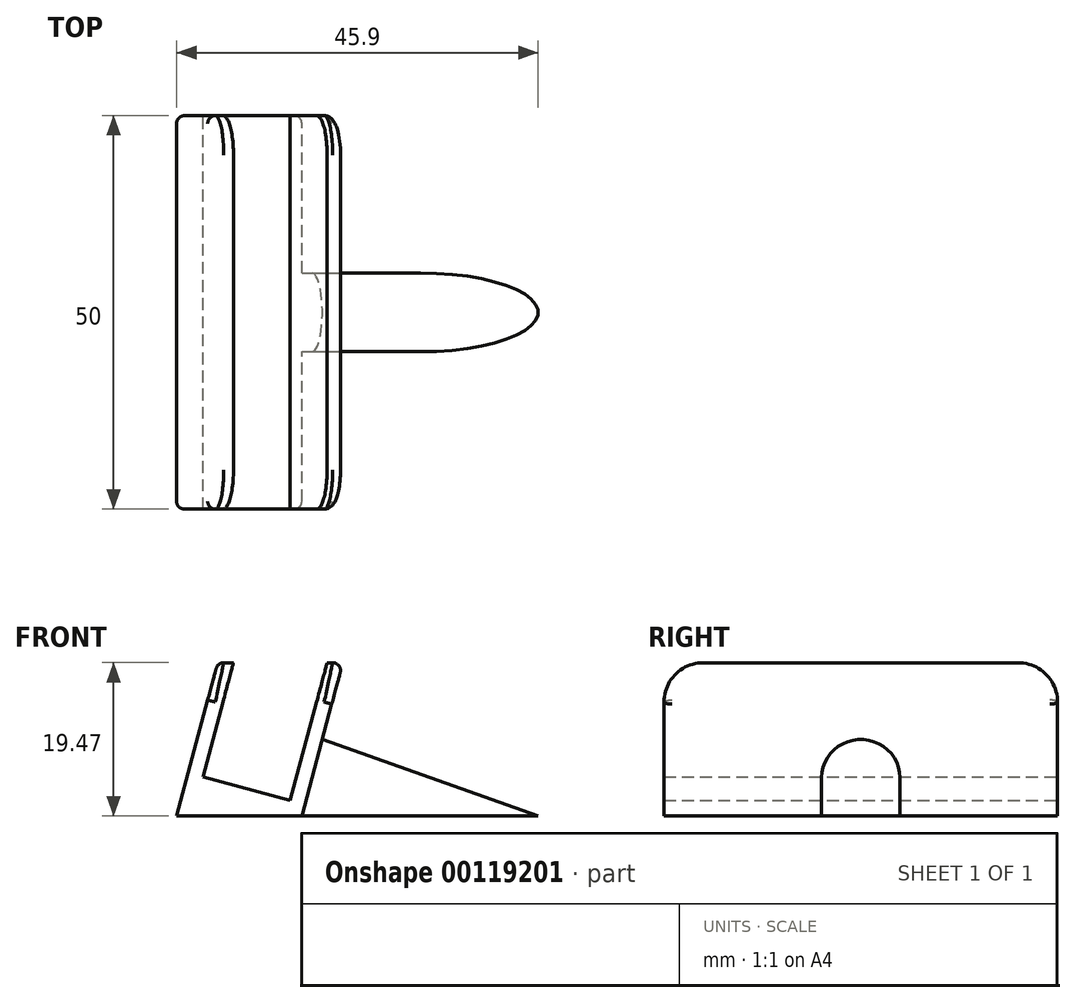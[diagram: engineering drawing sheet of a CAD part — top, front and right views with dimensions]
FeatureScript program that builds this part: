
annotation { "Feature Type Name" : "Feature", "Feature Type Description" : "" }
export const myFeature = defineFeature(function(context is Context, id is Id, definition is map)
    precondition{}
    {
        {
            var Q0;
            Q0=qCreatedBy(makeId("Front.planeOp"),FACE);
            var sketch = newSketch(context, id + "F0", { "sketchPlane" : qUnion([Q0])});
            skLineSegment(sketch, "E0", {"start": v(0, 0) * mm, "end": v(-11.1, 2.98) * mm});
            skLineSegment(sketch, "E1", {"start": v(-11.1, 2.98) * mm, "end": v(-7.23, 17.47) * mm});
            skLineSegment(sketch, "E2", {"start": v(-7.23, 17.47) * mm, "end": v(-9.23, 17.47) * mm});
            skLineSegment(sketch, "E3", {"start": v(-9.23, 17.47) * mm, "end": v(-13.9, 0) * mm});
            skLineSegment(sketch, "E4", {"start": v(4.68, 17.47) * mm, "end": v(6.68, 17.47) * mm});
            skLineSegment(sketch, "E5", {"start": v(4.68, 17.47) * mm, "end": v(0, 0) * mm});
            skLineSegment(sketch, "E6", {"start": v(-13.9, 0) * mm, "end": v(-14.44, -2) * mm});
            skLineSegment(sketch, "E7", {"start": v(-14.44, -2) * mm, "end": v(1.46, -2) * mm});
            skLineSegment(sketch, "E8", {"start": v(1.46, -2) * mm, "end": v(6.68, 17.47) * mm});
            skLineSegment(sketch, "E9", {"start": v(1.46, -2) * mm, "end": v(31.46, -2) * mm});
            skLineSegment(sketch, "E10", {"start": v(4.07, 7.73) * mm, "end": v(31.46, -2) * mm});
            skSolve(sketch);
        }
        {
            var Q0;
            Q0=makeQuery(id+"F0.imprint","IMPRINT",FACE,{"disambiguationData":[TD([[makeQuery(id+"F0.imprint","IMPRINT",EDGE,{"derivedFrom":sQuery(id+"F0.wireOp",EDGE,"E0")}),1.0]])]});
            extrude(context, id + "F1", {"entities" : qUnion([Q0]), "endBound" : BoundingType.SYMMETRIC, "depth" : 50 * mm});
        }
        {
            var Q0;
            {var subQ0=sQuery(id+"F0.wireOp",EDGE,"E9");Q0=makeQuery(id+"F0.imprint","IMPRINT",FACE,{"disambiguationData":[TD([[makeQuery(id+"F0.imprint","IMPRINT",EDGE,{"derivedFrom":subQ0}),1.0]])]});}
            extrude(context, id + "F2", {"entities" : qUnion([Q0]), "operationType" : NewBodyOperationType.ADD, "endBound" : BoundingType.SYMMETRIC, "depth" : 10 * mm});
        }
        {
            var Q0;
            Q0=makeQuery(id+"F2.opExtrude","CAP_EDGE",EDGE,{"disambiguationData":[OSD([sQuery(id+"F0.wireOp",EDGE,"E8")])],"isStart":false});
            var Q1;
            Q1=makeQuery(id+"F2.opExtrude","SWEPT_EDGE",EDGE,{"disambiguationData":[OSD([sQuery(id+"F0.wireOp",EDGE,"E8"),sQuery(id+"F0.wireOp",EDGE,"E10")])]});
            var Q2;
            Q2=makeQuery(id+"F2.opExtrude","CAP_EDGE",EDGE,{"disambiguationData":[OSD([sQuery(id+"F0.wireOp",EDGE,"E8")])],"isStart":true});
            var Q3;
            Q3=makeQuery(id+"F2.opExtrude","CAP_EDGE",EDGE,{"disambiguationData":[OSD([sQuery(id+"F0.wireOp",EDGE,"E10")])],"isStart":true});
            var Q4;
            Q4=makeQuery(id+"F2.opExtrude","CAP_EDGE",EDGE,{"disambiguationData":[OSD([sQuery(id+"F0.wireOp",EDGE,"E10")])],"isStart":false});
            var Q5;
            Q5=makeQuery(id+"F1.opExtrude","CAP_EDGE",EDGE,{"disambiguationData":[OSD([sQuery(id+"F0.wireOp",EDGE,"E4")])],"isStart":false});
            var Q6;
            Q6=makeQuery(id+"F1.opExtrude","CAP_EDGE",EDGE,{"disambiguationData":[OSD([sQuery(id+"F0.wireOp",EDGE,"E2")])],"isStart":false});
            var Q7;
            Q7=makeQuery(id+"F1.opExtrude","CAP_EDGE",EDGE,{"disambiguationData":[OSD([sQuery(id+"F0.wireOp",EDGE,"E2")])],"isStart":true});
            var Q8;
            Q8=makeQuery(id+"F1.opExtrude","CAP_EDGE",EDGE,{"disambiguationData":[OSD([sQuery(id+"F0.wireOp",EDGE,"E4")])],"isStart":true});
            fillet(context, id + "F3", {"entities" : qUnion([Q0, Q1, Q2, Q3, Q4, Q5, Q6, Q7, Q8]), "radius" : 5 * mm, "tangentPropagation" : true, "allowEdgeOverflow" : false});
        }
        {
            var Q0;
            Q0=makeQuery(id+"F1.opExtrude","SWEPT_EDGE",EDGE,{"disambiguationData":[OSD([sQuery(id+"F0.wireOp",EDGE,"E2"),sQuery(id+"F0.wireOp",EDGE,"E3")])]});
            var Q1;
            Q1=makeQuery(id+"F1.opExtrude","SWEPT_EDGE",EDGE,{"disambiguationData":[OSD([sQuery(id+"F0.wireOp",EDGE,"E4"),sQuery(id+"F0.wireOp",EDGE,"E8")])]});
            fillet(context, id + "F4", {"entities" : qUnion([Q0, Q1]), "radius" : 1 * mm, "tangentPropagation" : true, "allowEdgeOverflow" : false});
        }
    });
